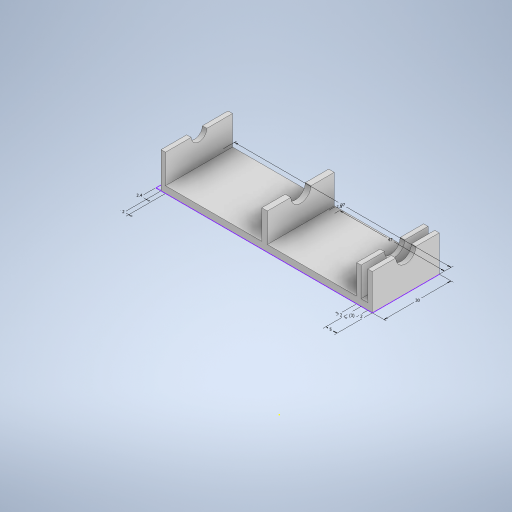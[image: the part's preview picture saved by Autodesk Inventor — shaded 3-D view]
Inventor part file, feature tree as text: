
AUTODESK INVENTOR PART (.ipt)
format: ipt  version: 2023.2 (Build 272271000, 271)  size: 648,192 bytes
history: native  units: mm
features: extrude x8, sketch x3, projected_geometry x1
ambient origin geometry x8: Origin, YZ Plane, XZ Plane, XY Plane, X Axis, Y Axis, Z Axis, Center Point
bodies: Solid1 (feature_tree)
feature tree (12):
  sketch  "Sketch1"  dims[d0=97.0mm d1=30.0mm]
  extrude  "Extrusion1"  Depth=30.0mm
  extrude  "Extrusion2"  Depth=2.0mm
  extrude  "Extrusion8"  Depth=2.0mm
  extrude  "Extrusion4"  Depth=3.0mm TaperAngle=0.0deg
  extrude  "Extrusion5"  Depth=16.0mm TaperAngle=0.0deg
  extrude  "Extrusion9"  Depth=16.0mm TaperAngle=0.0deg
  extrude  "Extrusion6"  Depth=3.0mm TaperAngle=0.0deg
  extrude  "Extrusion7"  Depth=3.0mm TaperAngle=0.0deg
  sketch  "Sketch2"  dims[d2=2.4mm d3=2.0mm]
  projected_geometry  "Projected Loop1"
  sketch  "Sketch3"  dims[d4=5.0mm d5=2.0mm d6=3.0mm d7=0.0mm d8=16.0mm d9=0.0mm d12=16.0mm d13=0.0mm d14=3.0mm d15=0.0mm d16=3.0mm d17=0.0mm d18=9.0mm d19=7.0mm d20=10.0mm d21=0.0mm d24=47.0mm d25=2.5mm d26=16.0mm d27=0.0mm d28=2.0mm d29=3.0mm d30=16.0mm d31=0.0mm d22=0.872665mm]
